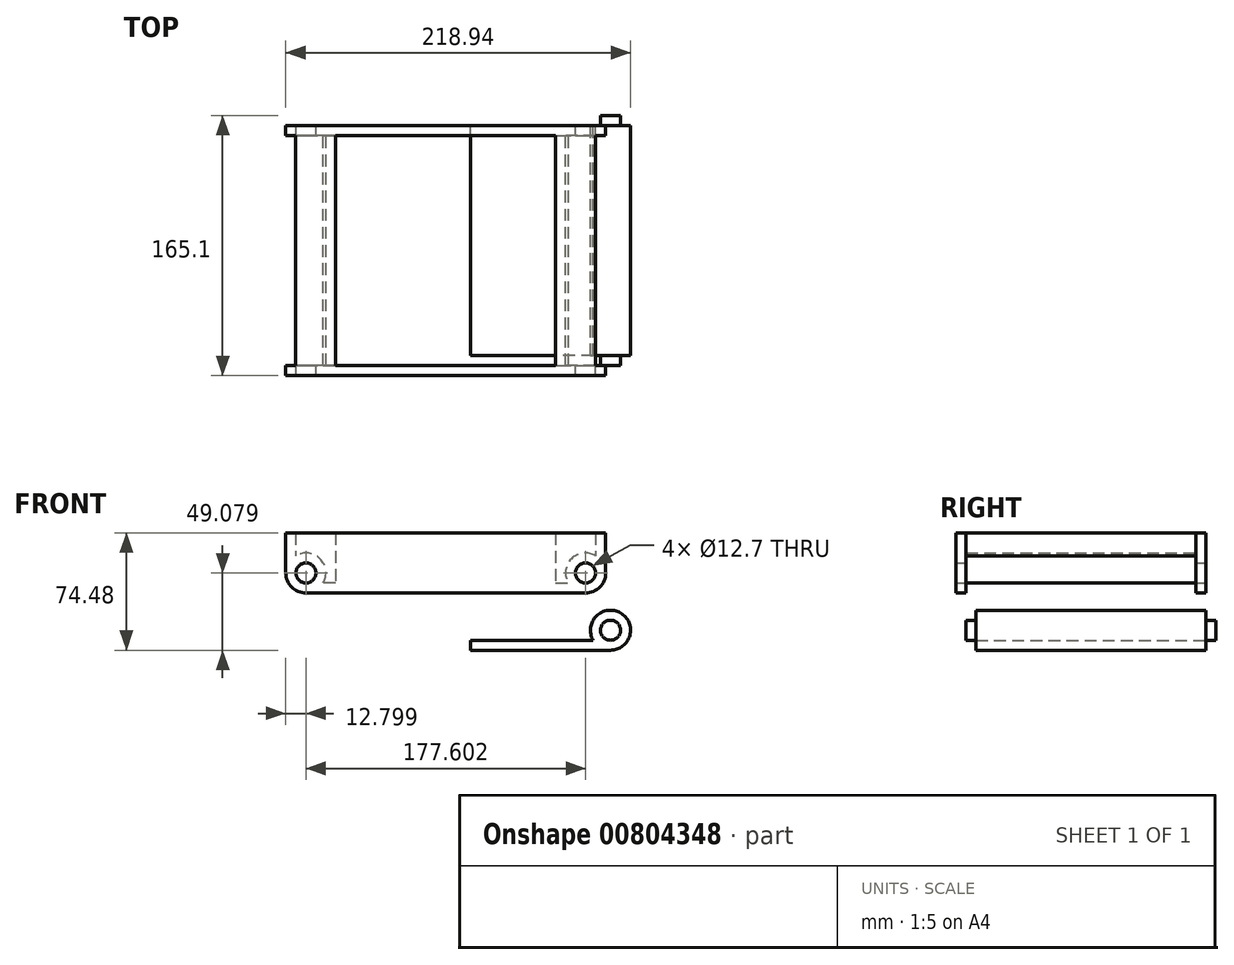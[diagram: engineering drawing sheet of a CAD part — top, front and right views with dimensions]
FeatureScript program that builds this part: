
annotation { "Feature Type Name" : "Feature", "Feature Type Description" : "" }
export const myFeature = defineFeature(function(context is Context, id is Id, definition is map)
    precondition{}
    {
        {
            var Q0;
            Q0=qCreatedBy(makeId("Front.planeOp"),FACE);
            cPlane(context, id + "F0", {"entities" : qUnion([Q0]), "cplaneType" : CPlaneType.OFFSET, "offset" : 76.2 * mm, "oppositeDirection" : true, "width" : 152.4 * mm, "height" : 152.4 * mm});
        }
        {
            var Q0;
            Q0=qCreatedBy(id+"F0.planeOp",FACE);
            var sketch = newSketch(context, id + "F1", { "sketchPlane" : qUnion([Q0])});
            skLineSegment(sketch, "E0.bottom", {"start": v(-95.81, 19.36) * mm, "end": v(107.39, 19.36) * mm});
            skLineSegment(sketch, "E0.right", {"start": v(107.39, 19.36) * mm, "end": v(107.39, -6.04) * mm});
            skCircle(sketch, "E1", {"center": v(94.6, -6.04) * mm, "radius": 6.35 * mm});
            skLineSegment(sketch, "E2.1.0.1", {"start": v(-95.81, 19.36) * mm, "end": v(-95.81, -6.04) * mm});
            skCircle(sketch, "E3", {"center": v(-83.01, -6.04) * mm, "radius": 6.35 * mm});
            skArc(sketch, "E4", {"start": v(94.6, -18.84) * mm, "mid": v(103.64, -15.1) * mm, "end": v(107.39, -6.04) * mm});
            skArc(sketch, "E5", {"start": v(-95.81, -6.04) * mm, "mid": v(-92.06, -15.1) * mm, "end": v(-83.01, -18.84) * mm});
            skLineSegment(sketch, "E6.bottom", {"start": v(-95.81, 19.36) * mm, "end": v(-89.46, 19.36) * mm});
            skLineSegment(sketch, "E6.right", {"start": v(-89.46, 19.36) * mm, "end": v(-89.46, 4.9) * mm});
            skLineSegment(sketch, "E7.top", {"start": v(-64.06, -12.49) * mm, "end": v(-72.07, -12.49) * mm});
            skArc(sketch, "E8", {"start": v(-72.07, -12.49) * mm, "mid": v(-74.03, 2.94) * mm, "end": v(-89.46, 4.9) * mm});
            skLineSegment(sketch, "E9", {"start": v(-64.06, 19.36) * mm, "end": v(-64.06, -12.49) * mm});
            skLineSegment(sketch, "E10.trimOffspring", {"start": v(-83.01, -18.84) * mm, "end": v(94.6, -18.84) * mm});
            skLineSegment(sketch, "E11.MirrorCS", {"start": v(75.64, 19.36) * mm, "end": v(75.64, -12.49) * mm});
            skLineSegment(sketch, "E12.MirrorCS", {"start": v(75.64, -12.49) * mm, "end": v(83.65, -12.49) * mm});
            skArc(sketch, "E13.MirrorCS", {"start": v(83.65, -12.49) * mm, "mid": v(85.61, 2.94) * mm, "end": v(101.04, 4.9) * mm});
            skLineSegment(sketch, "E14.MirrorCS", {"start": v(101.04, 19.36) * mm, "end": v(101.04, 4.9) * mm});
            skSolve(sketch);
        }
        {
            var Q0;
            {var subQ3=sQuery(id+"F1.wireOp",EDGE,"E0.right");Q0=makeQuery(id+"F1.imprint","IMPRINT",FACE,{"disambiguationData":[TD([[makeQuery(id+"F1.imprint","IMPRINT",EDGE,{"derivedFrom":subQ3}),-1.0]])]});}
            extrude(context, id + "F2", {"entities" : qUnion([Q0]), "depth" : 6.35 * mm, "offsetDistance" : 25.4 * mm});
        }
        {
            var Q0;
            {var subQ0=sQuery(id+"F1.wireOp",EDGE,"E6.right");Q0=makeQuery(id+"F1.imprint","IMPRINT",FACE,{"disambiguationData":[TD([[makeQuery(id+"F1.imprint","IMPRINT",EDGE,{"derivedFrom":subQ0}),1.0]])]});}
            extrude(context, id + "F3", {"entities" : qUnion([Q0]), "operationType" : NewBodyOperationType.ADD, "depth" : 152.4 * mm, "offsetDistance" : 25.4 * mm});
        }
        {
            var Q0;
            {var subQ0=sQuery(id+"F1.wireOp",EDGE,"E11.MirrorCS");Q0=makeQuery(id+"F1.imprint","IMPRINT",FACE,{"disambiguationData":[TD([[makeQuery(id+"F1.imprint","IMPRINT",EDGE,{"derivedFrom":subQ0}),1.0]])]});}
            extrude(context, id + "F4", {"entities" : qUnion([Q0]), "operationType" : NewBodyOperationType.ADD, "depth" : 152.4 * mm, "offsetDistance" : 25.4 * mm});
        }
        {
            var Q0;
            Q0=qCreatedBy(makeId("Front.planeOp"),FACE);
            cPlane(context, id + "F5", {"entities" : qUnion([Q0]), "cplaneType" : CPlaneType.OFFSET, "offset" : 76.2 * mm, "width" : 152.4 * mm, "height" : 152.4 * mm});
        }
        {
            var Q0;
            Q0=qCreatedBy(id+"F5.planeOp",FACE);
            var sketch = newSketch(context, id + "F6", { "sketchPlane" : qUnion([Q0])});
            skLineSegment(sketch, "E15.bottom", {"start": v(-95.81, 19.36) * mm, "end": v(107.39, 19.36) * mm});
            skLineSegment(sketch, "E15.right", {"start": v(107.39, 19.36) * mm, "end": v(107.39, -6.04) * mm});
            skCircle(sketch, "E16", {"center": v(94.6, -6.04) * mm, "radius": 6.35 * mm});
            skLineSegment(sketch, "E17.1.0.1", {"start": v(-95.81, 19.36) * mm, "end": v(-95.81, -6.04) * mm});
            skCircle(sketch, "E18", {"center": v(-83.01, -6.04) * mm, "radius": 6.35 * mm});
            skArc(sketch, "E19", {"start": v(94.6, -18.84) * mm, "mid": v(103.64, -15.1) * mm, "end": v(107.39, -6.04) * mm});
            skArc(sketch, "E20", {"start": v(-95.81, -6.04) * mm, "mid": v(-92.06, -15.1) * mm, "end": v(-83.01, -18.84) * mm});
            skLineSegment(sketch, "E21.bottom", {"start": v(-95.81, 19.36) * mm, "end": v(-89.46, 19.36) * mm});
            skLineSegment(sketch, "E22.trimOffspring", {"start": v(-83.01, -18.84) * mm, "end": v(94.6, -18.84) * mm});
            skSolve(sketch);
        }
        {
            var Q0;
            Q0=makeQuery(id+"F6.imprint","IMPRINT",FACE,{"disambiguationData":[TD([[makeQuery(id+"F6.imprint","IMPRINT",EDGE,{"derivedFrom":sQuery(id+"F6.wireOp",EDGE,"E15.bottom")}),-1.0]])]});
            extrude(context, id + "F7", {"entities" : qUnion([Q0]), "operationType" : NewBodyOperationType.ADD, "depth" : 6.35 * mm, "offsetDistance" : 25.4 * mm});
        }
        {
            var Q0;
            Q0=qCreatedBy(id+"F0.planeOp",FACE);
            var sketch = newSketch(context, id + "F8", { "sketchPlane" : qUnion([Q0])});
            skArc(sketch, "E23", {"start": v(110.43, -55.12) * mm, "mid": v(116.78, -31.42) * mm, "end": v(99.43, -48.77) * mm});
            skLineSegment(sketch, "E24.bottom", {"start": v(110.43, -55.12) * mm, "end": v(21.53, -55.12) * mm});
            skLineSegment(sketch, "E24.top", {"start": v(99.43, -48.77) * mm, "end": v(21.53, -48.77) * mm});
            skLineSegment(sketch, "E24.right", {"start": v(21.53, -55.12) * mm, "end": v(21.53, -48.77) * mm});
            skCircle(sketch, "E25", {"center": v(110.43, -42.42) * mm, "radius": 6.35 * mm});
            skSolve(sketch);
        }
        {
            var Q0;
            Q0=makeQuery(id+"F8.imprint","IMPRINT",FACE,{"disambiguationData":[TD([[makeQuery(id+"F8.imprint","IMPRINT",EDGE,{"derivedFrom":sQuery(id+"F8.wireOp",EDGE,"E23")}),1.0]])]});
            extrude(context, id + "F9", {"entities" : qUnion([Q0]), "depth" : 146.05 * mm, "offsetDistance" : 25.4 * mm});
        }
        {
            var Q0;
            Q0=makeQuery(id+"F8.imprint","IMPRINT",FACE,{"disambiguationData":[TD([[makeQuery(id+"F8.imprint","IMPRINT",EDGE,{"derivedFrom":sQuery(id+"F8.wireOp",EDGE,"E25")}),1.0]])]});
            var Q1;
            Q1=sQuery(id+"F8.wireOp",EDGE,"E25");
            extrude(context, id + "F10", {"entities" : qUnion([Q0]), "operationType" : NewBodyOperationType.ADD, "surfaceOperationType" : NewSurfaceOperationType.ADD, "surfaceEntities" : qUnion([Q1]), "depth" : 152.4 * mm, "offsetDistance" : 25.4 * mm, "hasSecondDirection" : true, "secondDirectionOppositeDirection" : true, "secondDirectionDepth" : 6.35 * mm});
        }
    });
